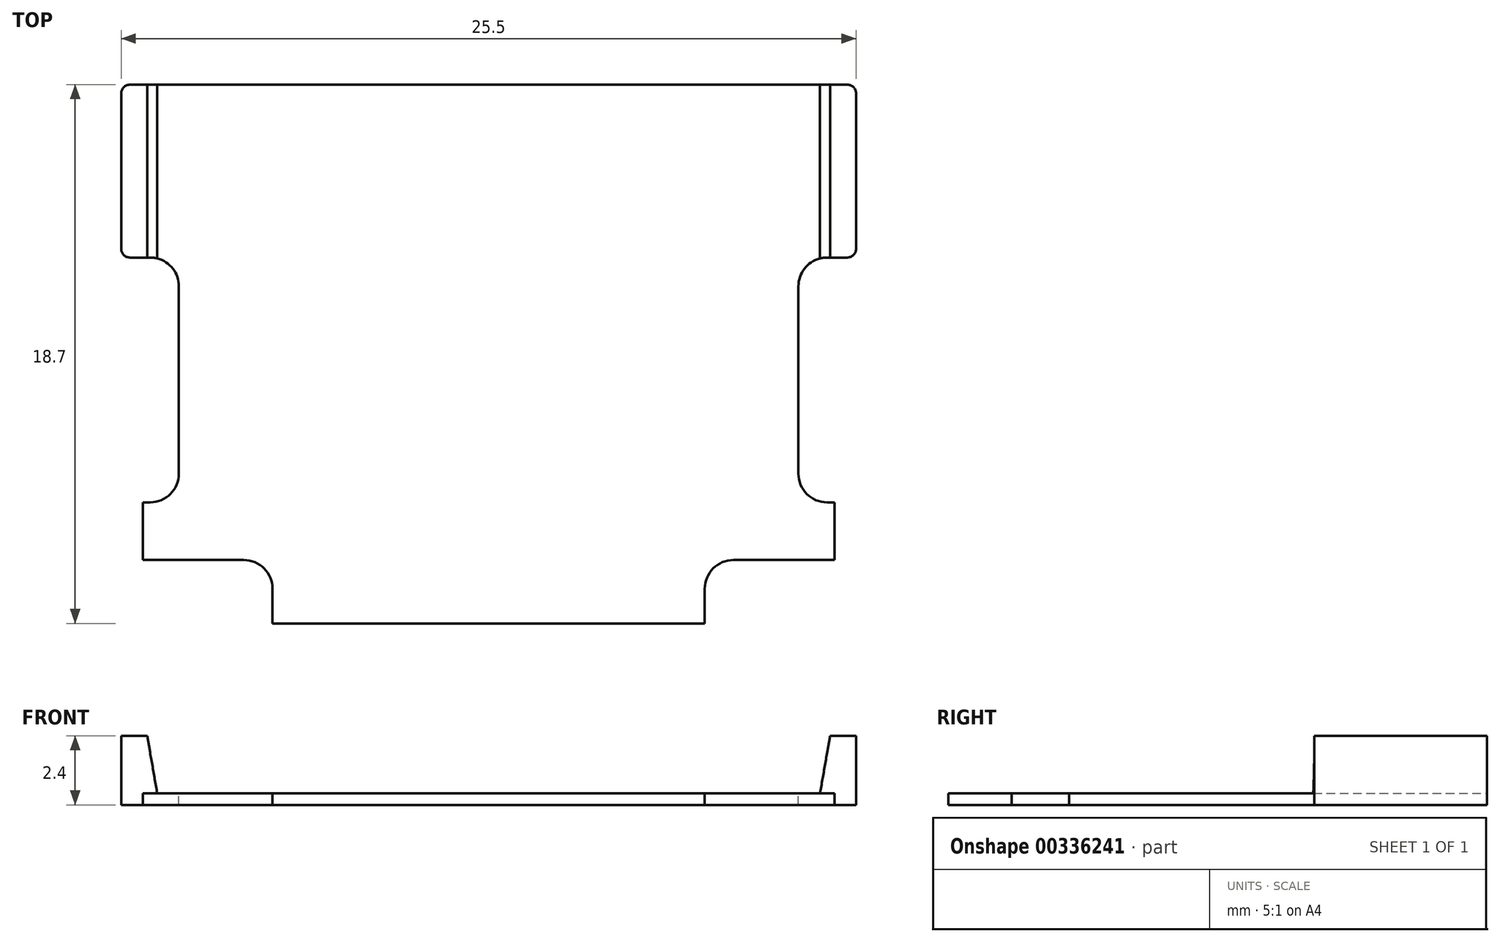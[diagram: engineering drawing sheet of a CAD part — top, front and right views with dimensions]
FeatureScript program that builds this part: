
annotation { "Feature Type Name" : "Feature", "Feature Type Description" : "" }
export const myFeature = defineFeature(function(context is Context, id is Id, definition is map)
    precondition{}
    {
        {
            var Q0;
            Q0=qCreatedBy(makeId("Top.planeOp"),FACE);
            var sketch = newSketch(context, id + "F0", { "sketchPlane" : qUnion([Q0])});
            skLineSegment(sketch, "E0.bottom", {"start": v(-10.75, 0) * mm, "end": v(10.75, 0) * mm});
            skLineSegment(sketch, "E0.top", {"start": v(-10.75, 16.5) * mm, "end": v(10.75, 16.5) * mm});
            skLineSegment(sketch, "E0.left", {"start": v(-10.75, 0) * mm, "end": v(-10.75, 16.5) * mm});
            skLineSegment(sketch, "E0.right", {"start": v(10.75, 0) * mm, "end": v(10.75, 16.5) * mm});
            skLineSegment(sketch, "E1", {"start": v(-10.75, 0) * mm, "end": v(-12, 0) * mm});
            skLineSegment(sketch, "E2", {"start": v(-12, 0) * mm, "end": v(-12, 2) * mm});
            skLineSegment(sketch, "E3", {"start": v(-12, 2) * mm, "end": v(-10.75, 2) * mm});
            skLineSegment(sketch, "E4.MirrorCS", {"start": v(12, 2) * mm, "end": v(10.75, 2) * mm});
            skLineSegment(sketch, "E5.MirrorCS", {"start": v(12, 0) * mm, "end": v(12, 2) * mm});
            skLineSegment(sketch, "E6.MirrorCS", {"start": v(10.75, 0) * mm, "end": v(12, 0) * mm});
            skLineSegment(sketch, "E7", {"start": v(-10.75, 2) * mm, "end": v(10.75, 2) * mm, "construction": true});
            skLineSegment(sketch, "E8", {"start": v(-10.75, 16.5) * mm, "end": v(-11.85, 16.5) * mm});
            skLineSegment(sketch, "E9", {"start": v(-11.85, 16.5) * mm, "end": v(-11.85, 10.5) * mm});
            skLineSegment(sketch, "E10", {"start": v(-11.85, 10.5) * mm, "end": v(-10.75, 10.5) * mm});
            skLineSegment(sketch, "E11", {"start": v(-11.85, 16.5) * mm, "end": v(-12.75, 16.5) * mm});
            skLineSegment(sketch, "E12", {"start": v(-12.75, 16.5) * mm, "end": v(-12.75, 10.5) * mm});
            skLineSegment(sketch, "E13", {"start": v(-12.75, 10.5) * mm, "end": v(-11.85, 10.5) * mm});
            skLineSegment(sketch, "E14.MirrorCS", {"start": v(10.75, 16.5) * mm, "end": v(11.85, 16.5) * mm});
            skLineSegment(sketch, "E15.MirrorCS", {"start": v(11.85, 10.5) * mm, "end": v(10.75, 10.5) * mm});
            skLineSegment(sketch, "E16.MirrorCS", {"start": v(11.85, 16.5) * mm, "end": v(11.85, 10.5) * mm});
            skLineSegment(sketch, "E17.MirrorCS", {"start": v(11.85, 16.5) * mm, "end": v(12.75, 16.5) * mm});
            skLineSegment(sketch, "E18.MirrorCS", {"start": v(12.75, 10.5) * mm, "end": v(11.85, 10.5) * mm});
            skLineSegment(sketch, "E19.MirrorCS", {"start": v(12.75, 16.5) * mm, "end": v(12.75, 10.5) * mm});
            skLineSegment(sketch, "E20", {"start": v(-10.75, 1) * mm, "end": v(10.75, 1) * mm});
            skPoint(sketch, "E20.startSnap0", {"position": v(-12, 1) * mm});
            skLineSegment(sketch, "E21", {"start": v(-7.5, 0) * mm, "end": v(-7.5, -1) * mm});
            skLineSegment(sketch, "E22", {"start": v(-7.5, -1) * mm, "end": v(7.5, -1) * mm});
            skLineSegment(sketch, "E23", {"start": v(7.5, -1) * mm, "end": v(7.5, 0) * mm});
            skLineSegment(sketch, "E24", {"start": v(-7.5, -1) * mm, "end": v(-7.5, -2.2) * mm});
            skLineSegment(sketch, "E25", {"start": v(-7.5, -2.2) * mm, "end": v(7.5, -2.2) * mm});
            skLineSegment(sketch, "E26", {"start": v(7.5, -2.2) * mm, "end": v(7.5, -1) * mm});
            skSolve(sketch);
        }
        {
            var Q0;
            Q0=qCreatedBy(makeId("Front.planeOp"),FACE);
            var sketch = newSketch(context, id + "F1", { "sketchPlane" : qUnion([Q0])});
            skLineSegment(sketch, "E27", {"start": v(0, 0) * mm, "end": v(0, 0.4) * mm});
            skLineSegment(sketch, "E28", {"start": v(0, 0.4) * mm, "end": v(0, 2.4) * mm});
            skSolve(sketch);
        }
        {
            var Q0;
            Q0=qSketchRegion(id+"F0",true);
            var Q1;
            Q1=sQuery(id+"F1.wireOp",EDGE,"E27");
            sweep(context, id + "F2", {"profiles" : qUnion([Q0]), "path" : qUnion([Q1])});
        }
        {
            var Q0;
            Q0=makeQuery(id+"F0.imprint","IMPRINT",FACE,{"disambiguationData":[TD([[makeQuery(id+"F0.imprint","IMPRINT",EDGE,{"derivedFrom":sQuery(id+"F0.wireOp",EDGE,"E16.MirrorCS")}),1.0]])]});
            var Q1;
            Q1=makeQuery(id+"F0.imprint","IMPRINT",FACE,{"disambiguationData":[TD([[makeQuery(id+"F0.imprint","IMPRINT",EDGE,{"derivedFrom":sQuery(id+"F0.wireOp",EDGE,"E9")}),-1.0]])]});
            var Q2;
            Q2=sQuery(id+"F1.wireOp",EDGE,"E27");
            var Q3;
            Q3=sQuery(id+"F1.wireOp",EDGE,"E28");
            sweep(context, id + "F3", {"operationType" : NewBodyOperationType.ADD, "profiles" : qUnion([Q0, Q1]), "path" : qUnion([Q2, Q3])});
        }
        {
            var Q0;
            {var subQ0=sQuery(id+"F1.wireOp",EDGE,"E27");var subQ1=sQuery(id+"F0.wireOp",EDGE,"E17.MirrorCS");var subQ2=sQuery(id+"F0.wireOp",EDGE,"E11");Q0=makeQuery(id+"F3.boolean.opBoolean","MERGE",FACE,{"derivedFrom":[makeQuery(id+"F2.opSweep","SWEPT_FACE",FACE,{"disambiguationData":[OSD([sQuery(id+"F0.wireOp",EDGE,"E0.top"),sQuery(id+"F0.wireOp",EDGE,"E8"),subQ2,sQuery(id+"F0.wireOp",EDGE,"E14.MirrorCS"),subQ1,subQ0])]}),makeQuery(id+"F3.opSweep","SWEPT_FACE",FACE,{"disambiguationData":[OSD([subQ2,subQ0])]}),makeQuery(id+"F3.opSweep","SWEPT_FACE",FACE,{"disambiguationData":[OSD([subQ1,subQ0])]})]});}
            var sketch = newSketch(context, id + "F4", { "sketchPlane" : qUnion([Q0])});
            skLineSegment(sketch, "E29", {"start": v(-11.5, 0.4) * mm, "end": v(11.5, 0.4) * mm, "construction": true});
            skLineSegment(sketch, "E30", {"start": v(-11.85, 2.4) * mm, "end": v(-11.85, 0.4) * mm});
            skLineSegment(sketch, "E31", {"start": v(-11.85, 0.4) * mm, "end": v(-11.5, 0.4) * mm});
            skLineSegment(sketch, "E32", {"start": v(-11.5, 0.4) * mm, "end": v(-11.85, 2.4) * mm});
            skLineSegment(sketch, "E33.MirrorCS", {"start": v(11.5, 0.4) * mm, "end": v(11.85, 2.4) * mm});
            skLineSegment(sketch, "E34.MirrorCS", {"start": v(11.85, 0.4) * mm, "end": v(11.5, 0.4) * mm});
            skLineSegment(sketch, "E35.MirrorCS", {"start": v(11.85, 2.4) * mm, "end": v(11.85, 0.4) * mm});
            skSolve(sketch);
        }
        {
            var Q0;
            Q0=qSketchRegion(id+"F4",true);
            var Q1;
            {var subQ0=sQuery(id+"F1.wireOp",EDGE,"E27");var subQ1=sQuery(id+"F0.wireOp",EDGE,"E18.MirrorCS");Q1=makeQuery(id+"F3.boolean.opBoolean","MERGE",FACE,{"derivedFrom":[makeQuery(id+"F2.opSweep","SWEPT_FACE",FACE,{"disambiguationData":[OSD([sQuery(id+"F0.wireOp",EDGE,"E15.MirrorCS"),subQ1,subQ0])]}),makeQuery(id+"F3.opSweep","SWEPT_FACE",FACE,{"disambiguationData":[OSD([subQ1,subQ0])]})]});}
            extrude(context, id + "F5", {"entities" : qUnion([Q0]), "operationType" : NewBodyOperationType.ADD, "endBound" : BoundingType.UP_TO_SURFACE, "oppositeDirection" : true, "depth" : 25 * mm, "endBoundEntityFace" : qUnion([Q1]), "offsetDistance" : 25 * mm});
        }
        {
            var Q0;
            Q0=makeQuery(id+"F2.opSweep","SWEPT_EDGE",EDGE,{"disambiguationData":[OSD([sQuery(id+"F0.wireOp",EDGE,"E0.bottom"),sQuery(id+"F0.wireOp",EDGE,"E23"),sQuery(id+"F1.wireOp",EDGE,"E27")])]});
            var Q1;
            Q1=makeQuery(id+"F2.opSweep","SWEPT_EDGE",EDGE,{"disambiguationData":[OSD([sQuery(id+"F0.wireOp",EDGE,"E0.bottom"),sQuery(id+"F0.wireOp",EDGE,"E21"),sQuery(id+"F1.wireOp",EDGE,"E27")])]});
            var Q2;
            Q2=makeQuery(id+"F2.opSweep","SWEPT_EDGE",EDGE,{"disambiguationData":[OSD([sQuery(id+"F0.wireOp",EDGE,"E0.right"),sQuery(id+"F0.wireOp",EDGE,"E15.MirrorCS"),sQuery(id+"F1.wireOp",EDGE,"E27")])]});
            var Q3;
            Q3=makeQuery(id+"F2.opSweep","SWEPT_EDGE",EDGE,{"disambiguationData":[OSD([sQuery(id+"F0.wireOp",EDGE,"E0.left"),sQuery(id+"F0.wireOp",EDGE,"E10"),sQuery(id+"F1.wireOp",EDGE,"E27")])]});
            var Q4;
            Q4=makeQuery(id+"F2.opSweep","SWEPT_EDGE",EDGE,{"disambiguationData":[OSD([sQuery(id+"F0.wireOp",EDGE,"E0.left"),sQuery(id+"F0.wireOp",EDGE,"E3"),sQuery(id+"F1.wireOp",EDGE,"E27")])]});
            var Q5;
            Q5=makeQuery(id+"F2.opSweep","SWEPT_EDGE",EDGE,{"disambiguationData":[OSD([sQuery(id+"F0.wireOp",EDGE,"E0.right"),sQuery(id+"F0.wireOp",EDGE,"E4.MirrorCS"),sQuery(id+"F1.wireOp",EDGE,"E27")])]});
            fillet(context, id + "F6", {"entities" : qUnion([Q0, Q1, Q2, Q3, Q4, Q5]), "radius" : 1 * mm, "allowEdgeOverflow" : false});
        }
        {
            var Q0;
            Q0=makeQuery(id+"F3.opSweep","SWEPT_EDGE",EDGE,{"disambiguationData":[OSD([sQuery(id+"F0.wireOp",EDGE,"E21"),sQuery(id+"F0.wireOp",EDGE,"E22"),sQuery(id+"F0.wireOp",EDGE,"E24"),sQuery(id+"F1.wireOp",EDGE,"E27")])]});
            var Q1;
            Q1=makeQuery(id+"F3.opSweep","SWEPT_EDGE",EDGE,{"disambiguationData":[OSD([sQuery(id+"F0.wireOp",EDGE,"E22"),sQuery(id+"F0.wireOp",EDGE,"E23"),sQuery(id+"F0.wireOp",EDGE,"E26"),sQuery(id+"F1.wireOp",EDGE,"E27")])]});
            fillet(context, id + "F7", {"entities" : qUnion([Q0, Q1]), "radius" : 0.3 * mm, "allowEdgeOverflow" : false});
        }
    });
